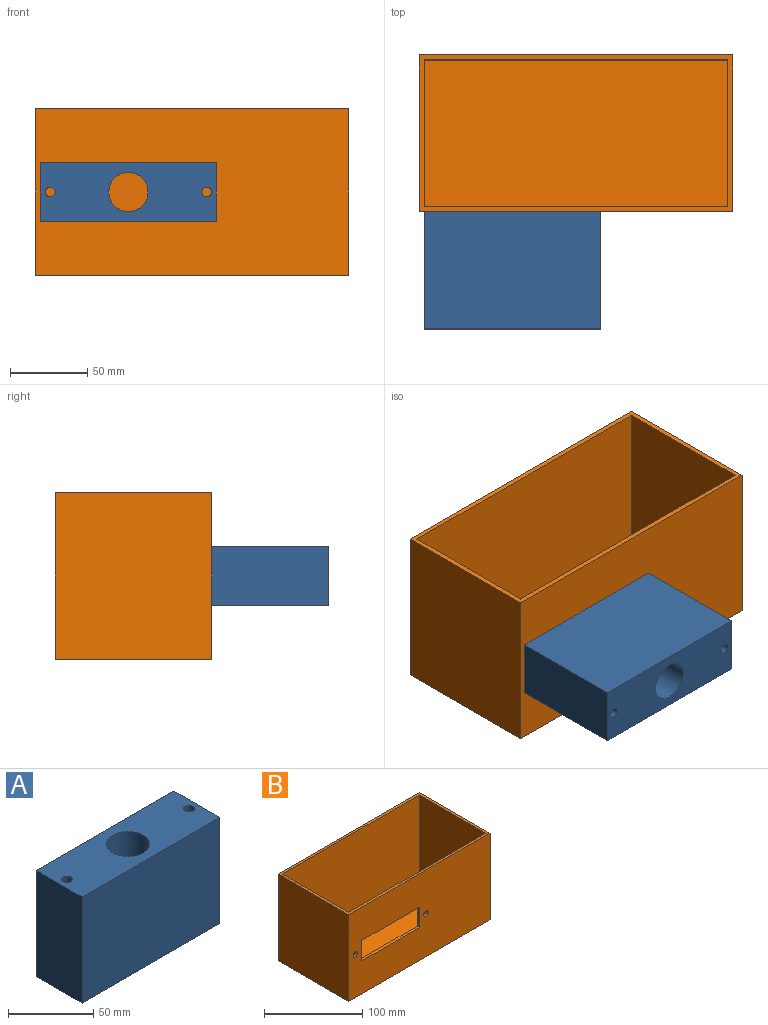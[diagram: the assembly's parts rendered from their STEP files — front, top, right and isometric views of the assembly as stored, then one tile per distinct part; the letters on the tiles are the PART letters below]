
ASSEMBLY  parts=2 mates=1
PART A: 9 faces, bbox 114.3x38.1x76.2 mm
  f0: plane 114.3x76.2mm, normal (0,1,0), area 8709.7mm2, adj f1,f3,f4,f5
  f1: plane 76.2x38.1mm, normal (-1,0,0), area 2903.2mm2, adj f0,f2,f4,f5
  f2: plane 114.3x76.2mm, normal (0,-1,0), area 8709.7mm2, adj f1,f3,f4,f5
  f3: plane 76.2x38.1mm, normal (1,0,0), area 2903.2mm2, adj f0,f2,f4,f5
  f4: plane 114.3x38.1mm, normal (0,0,1), area 3784.8mm2, adj f0,f1,f2,f3,f6,f7,f8
  f5: plane 114.3x38.1mm, normal (0,0,-1), area 3784.8mm2, adj f0,f1,f2,f3,f6,f7,f8
  f6: cylinder r=12.7mm len=76.2mm, axis (0,0,-1), area 6080.5mm2, adj f4,f5
  f7: cylinder r=3.17mm len=76.2mm, axis (0,0,-1), area 1520.1mm2, adj f4,f5
  f8: cylinder r=3.17mm len=76.2mm, axis (0,0,-1), area 1520.1mm2, adj f4,f5
PART B: 17 faces, bbox 203.2x101.6x108 mm
  f0: plane 203.2x107.95mm, normal (0,-1,0), area 19775.3mm2, adj f2,f4,f5,f6,f11,f12,f13,f14
  f1: plane 196.85x104.78mm, normal (0,1,0), area 18464.9mm2, adj f2,f8,f9,f10,f11,f12,f13,f14
  f2: plane 203.2x101.6mm, normal (0,0,1), area 1895.2mm2, adj f0,f1,f3,f4,f5,f7,f8,f9
  f3: plane 203.2x107.95mm, normal (0,1,0), area 21935.4mm2, adj f2,f4,f5,f6
  f4: plane 107.95x101.6mm, normal (-1,0,0), area 10967.7mm2, adj f0,f2,f3,f6
  f5: plane 107.95x101.6mm, normal (1,0,0), area 10967.7mm2, adj f0,f2,f3,f6
  f6: plane 203.2x101.6mm, normal (0,0,-1), area 20645.1mm2, adj f0,f3,f4,f5
  f7: plane 196.85x104.78mm, normal (0,-1,0), area 20625mm2, adj f2,f8,f9,f10
  f8: plane 104.78x95.25mm, normal (1,0,0), area 9979.8mm2, adj f1,f2,f7,f10
  f9: plane 104.78x95.25mm, normal (-1,0,0), area 9979.8mm2, adj f1,f2,f7,f10
  f10: plane 196.85x95.25mm, normal (0,0,1), area 18750mm2, adj f1,f7,f8,f9
  f11: plane 82.55x3.18mm, normal (0,0,-1), area 262.1mm2, adj f0,f1,f12,f14
  f12: plane 25.4x3.18mm, normal (1,0,0), area 80.6mm2, adj f0,f1,f11,f13
  f13: plane 82.55x3.18mm, normal (0,0,1), area 262.1mm2, adj f0,f1,f12,f14
  f14: plane 25.4x3.18mm, normal (-1,0,0), area 80.6mm2, adj f0,f1,f11,f13
  f15: cylinder r=3.17mm len=6.35mm, axis (0,-1,0), area 63.3mm2, adj f0,f1
  f16: cylinder r=3.17mm len=6.35mm, axis (0,-1,0), area 63.3mm2, adj f0,f1
PLACE A rot(axis=(1,0,0),90deg) t=(-6.97,23.89,37.39)mm
PLACE B t=(11.54,23.89,2.47)mm
MATE fastened A.f8 <-> B.f16  axis (0,1,0) through (73.71,23.89,56.44)mm
